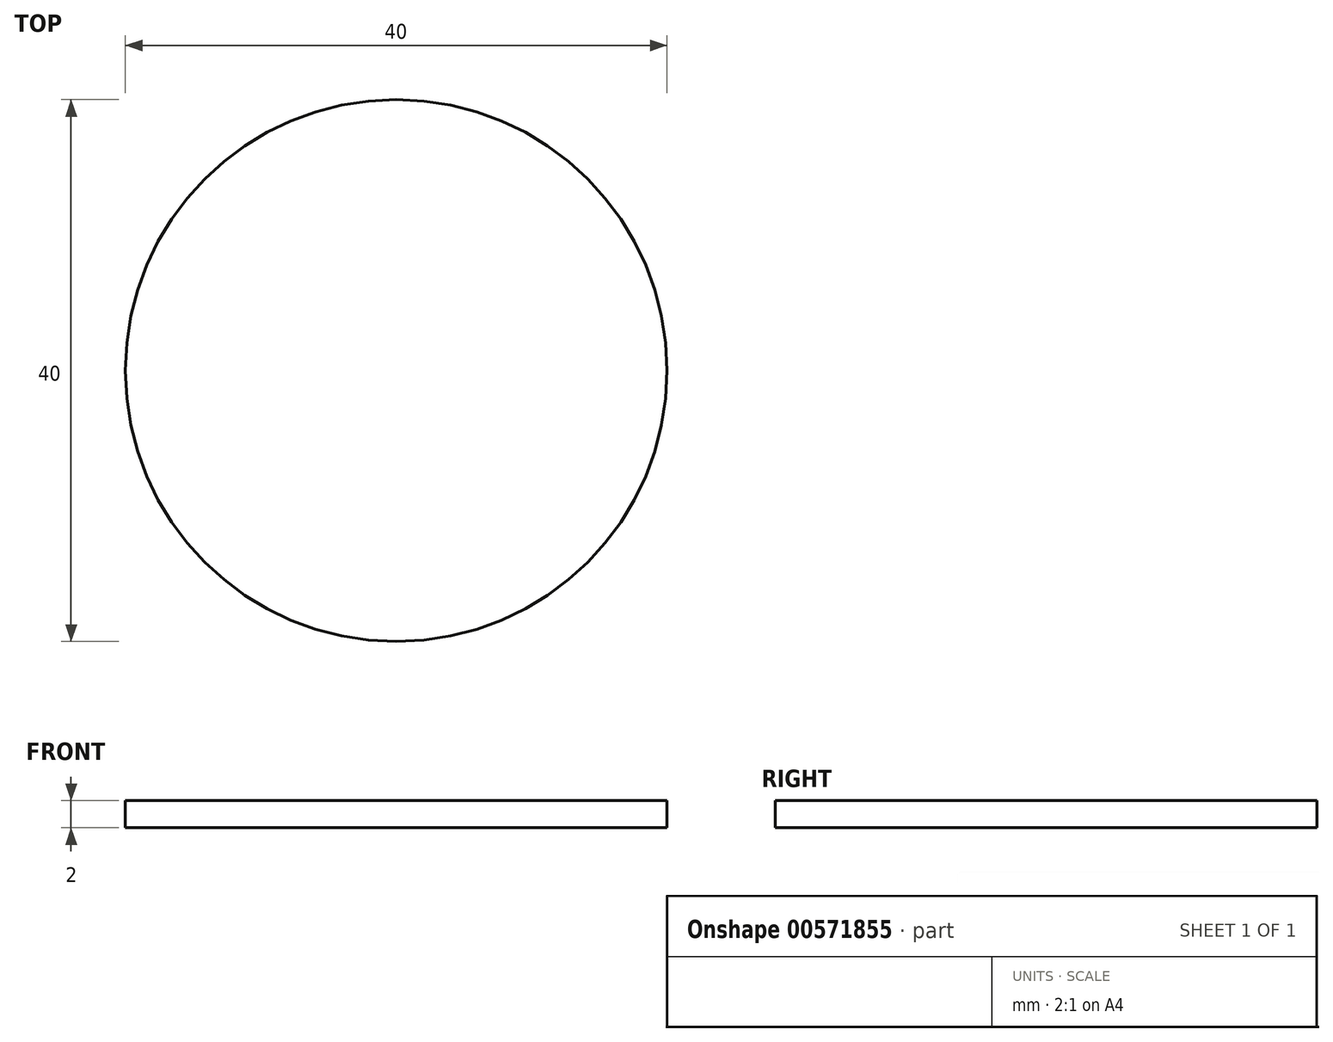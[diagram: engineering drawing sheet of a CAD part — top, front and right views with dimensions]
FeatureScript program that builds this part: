
annotation { "Feature Type Name" : "Feature", "Feature Type Description" : "" }
export const myFeature = defineFeature(function(context is Context, id is Id, definition is map)
    precondition{}
    {
        {
            var Q0;
            Q0=qCreatedBy(makeId("Top.planeOp"),FACE);
            var sketch = newSketch(context, id + "F0", { "sketchPlane" : qUnion([Q0])});
            skCircle(sketch, "E0", {"center": v(0, 0) * mm, "radius": 20 * mm});
            skSolve(sketch);
        }
        {
            var Q0;
            Q0 = qSketchRegion(id + "F0", true);
            extrude(context, id + "F1", {"entities" : qUnion([Q0]), "depth" : 2 * mm, "offsetDistance" : 25.4 * mm});
        }
    });
